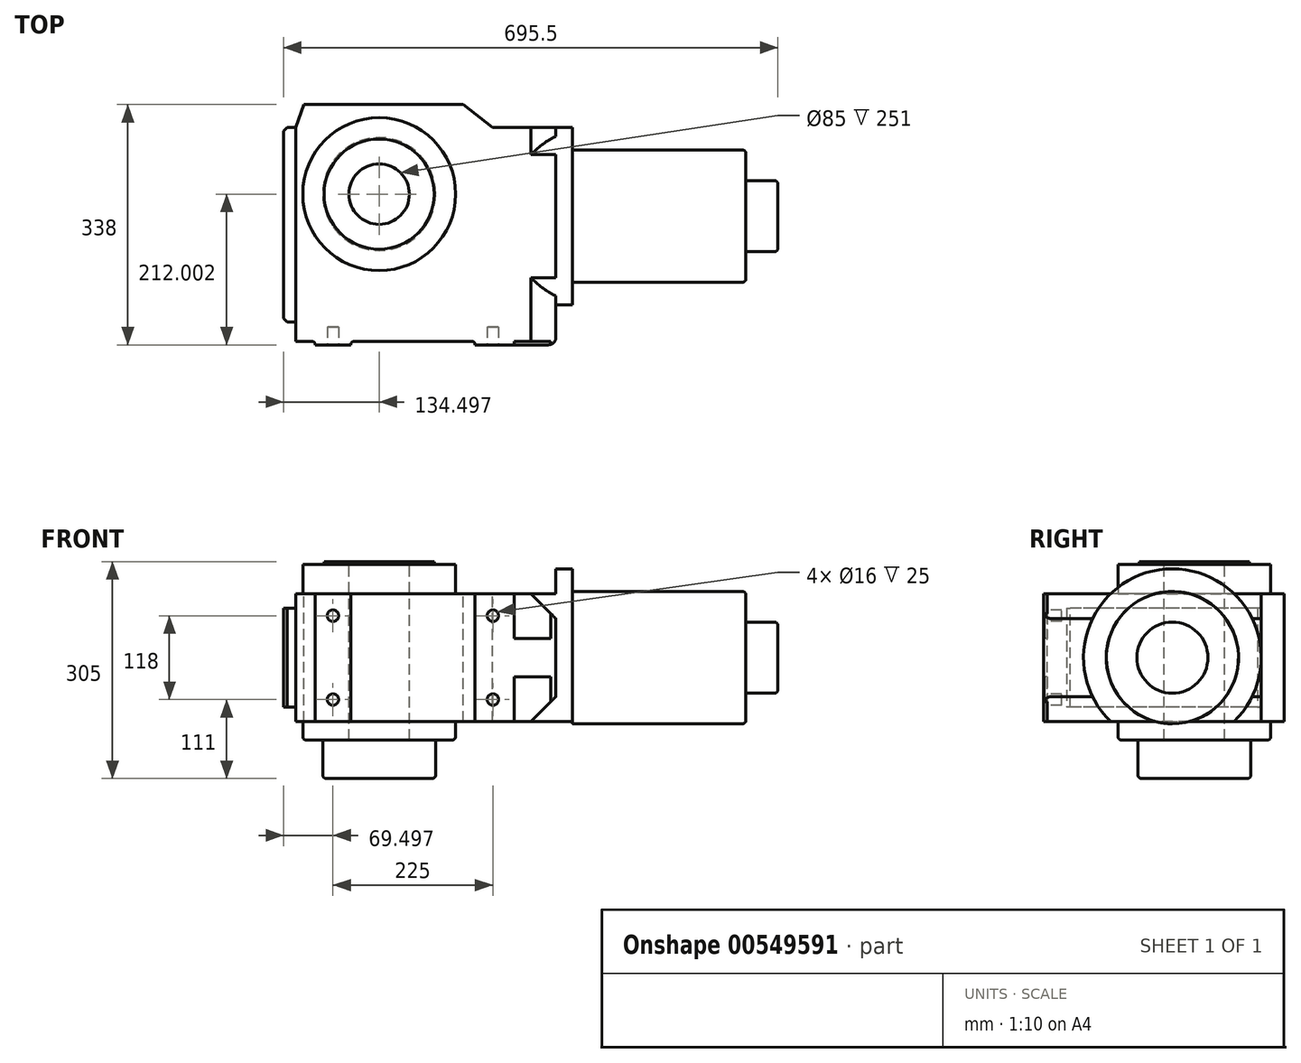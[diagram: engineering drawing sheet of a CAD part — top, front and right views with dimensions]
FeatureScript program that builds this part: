
annotation { "Feature Type Name" : "Feature", "Feature Type Description" : "" }
export const myFeature = defineFeature(function(context is Context, id is Id, definition is map)
    precondition{}
    {
        {
            var Q0;
            Q0=qCreatedBy(makeId("Top.planeOp"),FACE);
            var sketch = newSketch(context, id + "F0", { "sketchPlane" : qUnion([Q0])});
            skLineSegment(sketch, "E0.bottom", {"start": v(-178.5, 191.18) * mm, "end": v(187.5, 191.18) * mm});
            skLineSegment(sketch, "E0.top", {"start": v(-178.5, -146.82) * mm, "end": v(187.5, -146.82) * mm});
            skLineSegment(sketch, "E0.left", {"start": v(-178.5, 191.18) * mm, "end": v(-178.5, -146.82) * mm});
            skLineSegment(sketch, "E0.right", {"start": v(187.5, 191.18) * mm, "end": v(187.5, -146.82) * mm});
            skSolve(sketch);
        }
        {
            var Q0;
            Q0=makeQuery(id+"F0.imprint","IMPRINT",FACE,{"disambiguationData":[TD([[makeQuery(id+"F0.imprint","IMPRINT",EDGE,{"derivedFrom":sQuery(id+"F0.wireOp",EDGE,"E0.bottom")}),-1.0]])]});
            extrude(context, id + "F1", {"entities" : qUnion([Q0]), "oppositeDirection" : true, "depth" : 180 * mm, "offsetDistance" : 25 * mm});
        }
        {
            var Q0;
            Q0=makeQuery(id+"F1.opExtrude","CAP_FACE",FACE,{"disambiguationData":[OSD([sQuery(id+"F0.wireOp",EDGE,"E0.bottom"),sQuery(id+"F0.wireOp",EDGE,"E0.top"),sQuery(id+"F0.wireOp",EDGE,"E0.left"),sQuery(id+"F0.wireOp",EDGE,"E0.right")])],"isStart":true});
            var sketch = newSketch(context, id + "F2", { "sketchPlane" : qUnion([Q0])});
            skLineSegment(sketch, "E1", {"start": v(-252.27, 65.18) * mm, "end": v(288.5, 65.18) * mm, "construction": true});
            skLineSegment(sketch, "E2", {"start": v(-61, 181.9) * mm, "end": v(-61, -151.05) * mm, "construction": true});
            skCircle(sketch, "E3", {"center": v(-61, 65.18) * mm, "radius": 107.5 * mm});
            skSolve(sketch);
        }
        {
            var Q0;
            Q0=makeQuery(id+"F2.imprint","IMPRINT",FACE,{"disambiguationData":[TD([[makeQuery(id+"F2.imprint","IMPRINT",EDGE,{"derivedFrom":sQuery(id+"F2.wireOp",EDGE,"E3")}),1.0]])]});
            extrude(context, id + "F3", {"entities" : qUnion([Q0]), "operationType" : NewBodyOperationType.ADD, "depth" : 41 * mm, "offsetDistance" : 25 * mm});
        }
        {
            var Q0;
            Q0=makeQuery(id+"F1.opExtrude","CAP_FACE",FACE,{"disambiguationData":[OSD([sQuery(id+"F0.wireOp",EDGE,"E0.bottom"),sQuery(id+"F0.wireOp",EDGE,"E0.top"),sQuery(id+"F0.wireOp",EDGE,"E0.left"),sQuery(id+"F0.wireOp",EDGE,"E0.right")])],"isStart":true});
            var sketch = newSketch(context, id + "F4", { "sketchPlane" : qUnion([Q0])});
            skLineSegment(sketch, "E4", {"start": v(-178.5, -141.82) * mm, "end": v(-151, -141.82) * mm});
            skLineSegment(sketch, "E5", {"start": v(-151, -141.82) * mm, "end": v(-151, -146.82) * mm});
            skLineSegment(sketch, "E6", {"start": v(-101, -146.82) * mm, "end": v(-101, -141.82) * mm});
            skLineSegment(sketch, "E7", {"start": v(-101, -141.82) * mm, "end": v(74, -141.82) * mm});
            skLineSegment(sketch, "E8", {"start": v(74, -141.82) * mm, "end": v(74, -146.82) * mm});
            skSolve(sketch);
        }
        {
            var Q0;
            {var subQ0=sQuery(id+"F4.wireOp",EDGE,"E4");Q0=makeQuery(id+"F4.imprint","IMPRINT",FACE,{"disambiguationData":[TD([[makeQuery(id+"F4.imprint","IMPRINT",EDGE,{"derivedFrom":subQ0}),-1.0]])]});}
            var Q1;
            {var subQ0=sQuery(id+"F4.wireOp",EDGE,"E6");Q1=makeQuery(id+"F4.imprint","IMPRINT",FACE,{"disambiguationData":[TD([[makeQuery(id+"F4.imprint","IMPRINT",EDGE,{"derivedFrom":subQ0}),-1.0]])]});}
            extrude(context, id + "F5", {"entities" : qUnion([Q0, Q1]), "operationType" : NewBodyOperationType.REMOVE, "endBound" : BoundingType.THROUGH_ALL, "oppositeDirection" : true, "depth" : 25 * mm, "offsetDistance" : 25 * mm});
        }
        {
            var Q0;
            {var subQ0=sQuery(id+"F0.wireOp",EDGE,"E0.right");var subQ2=sQuery(id+"F0.wireOp",EDGE,"E0.top");Q0=makeQuery(id+"F5.boolean.opBoolean","SPLIT",FACE,{"disambiguationData":[TD([makeQuery(id+"F1.opExtrude","SWEPT_FACE",FACE,{"disambiguationData":[OSD([subQ0])]})])],"derivedFrom":makeQuery(id+"F1.opExtrude","SWEPT_FACE",FACE,{"disambiguationData":[OSD([subQ2])]})});}
            var sketch = newSketch(context, id + "F6", { "sketchPlane" : qUnion([Q0])});
            skLineSegment(sketch, "E9.bottom", {"start": v(129, 0) * mm, "end": v(180.7, 0) * mm});
            skLineSegment(sketch, "E9.top", {"start": v(129, -63) * mm, "end": v(180.7, -63) * mm});
            skLineSegment(sketch, "E9.left", {"start": v(129, 0) * mm, "end": v(129, -63) * mm});
            skLineSegment(sketch, "E9.right", {"start": v(180.7, 0) * mm, "end": v(180.7, -63) * mm});
            skLineSegment(sketch, "E10.bottom", {"start": v(129, -117) * mm, "end": v(180.7, -117) * mm});
            skLineSegment(sketch, "E10.top", {"start": v(129, -180) * mm, "end": v(180.7, -180) * mm});
            skLineSegment(sketch, "E10.left", {"start": v(129, -117) * mm, "end": v(129, -180) * mm});
            skLineSegment(sketch, "E10.right", {"start": v(180.7, -117) * mm, "end": v(180.7, -180) * mm});
            skSolve(sketch);
        }
        {
            var Q0;
            Q0=makeQuery(id+"F6.imprint","IMPRINT",FACE,{"disambiguationData":[TD([[makeQuery(id+"F6.imprint","IMPRINT",EDGE,{"derivedFrom":sQuery(id+"F6.wireOp",EDGE,"E9.bottom")}),-1.0]])]});
            var Q1;
            Q1=makeQuery(id+"F6.imprint","IMPRINT",FACE,{"disambiguationData":[TD([[makeQuery(id+"F6.imprint","IMPRINT",EDGE,{"derivedFrom":sQuery(id+"F6.wireOp",EDGE,"E10.bottom")}),-1.0]])]});
            extrude(context, id + "F7", {"entities" : qUnion([Q0, Q1]), "operationType" : NewBodyOperationType.REMOVE, "oppositeDirection" : true, "depth" : 5 * mm, "offsetDistance" : 25 * mm});
        }
        {
            var Q0;
            Q0=makeQuery(id+"F5.boolean.opBoolean","COPY",EDGE,{"derivedFrom":makeQuery(id+"F5.opExtrude","SWEPT_EDGE",EDGE,{"disambiguationData":[OSD([sQuery(id+"F4.wireOp",EDGE,"E4"),sQuery(id+"F4.wireOp",EDGE,"E5")])]})});
            var Q1;
            Q1=makeQuery(id+"F5.boolean.opBoolean","COPY",EDGE,{"derivedFrom":makeQuery(id+"F5.opExtrude","SWEPT_EDGE",EDGE,{"disambiguationData":[OSD([sQuery(id+"F4.wireOp",EDGE,"E6"),sQuery(id+"F4.wireOp",EDGE,"E7")])]})});
            var Q2;
            Q2=makeQuery(id+"F5.boolean.opBoolean","COPY",EDGE,{"derivedFrom":makeQuery(id+"F5.opExtrude","SWEPT_EDGE",EDGE,{"disambiguationData":[OSD([sQuery(id+"F4.wireOp",EDGE,"E7"),sQuery(id+"F4.wireOp",EDGE,"E8")])]})});
            fillet(context, id + "F8", {"entities" : qUnion([Q0, Q1, Q2]), "radius" : 5 * mm, "tangentPropagation" : true, "allowEdgeOverflow" : false});
        }
        {
            var Q0;
            Q0=makeQuery(id+"F1.opExtrude","SWEPT_EDGE",EDGE,{"disambiguationData":[OSD([sQuery(id+"F0.wireOp",EDGE,"E0.top"),sQuery(id+"F0.wireOp",EDGE,"E0.right")])]});
            fillet(context, id + "F9", {"entities" : qUnion([Q0]), "radius" : 10 * mm, "tangentPropagation" : true, "allowEdgeOverflow" : false});
        }
        {
            var Q0;
            Q0=makeQuery(id+"F1.opExtrude","SWEPT_FACE",FACE,{"disambiguationData":[OSD([sQuery(id+"F0.wireOp",EDGE,"E0.left")])]});
            var sketch = newSketch(context, id + "F10", { "sketchPlane" : qUnion([Q0])});
            skLineSegment(sketch, "E11.bottom", {"start": v(-159.18, -20.5) * mm, "end": v(114.82, -20.5) * mm});
            skLineSegment(sketch, "E11.top", {"start": v(-159.18, -159.5) * mm, "end": v(114.82, -159.5) * mm});
            skLineSegment(sketch, "E11.left", {"start": v(-159.18, -20.5) * mm, "end": v(-159.18, -159.5) * mm});
            skLineSegment(sketch, "E11.right", {"start": v(114.82, -20.5) * mm, "end": v(114.82, -159.5) * mm});
            skSolve(sketch);
        }
        {
            var Q0;
            Q0=makeQuery(id+"F10.imprint","IMPRINT",FACE,{"disambiguationData":[TD([[makeQuery(id+"F10.imprint","IMPRINT",EDGE,{"derivedFrom":sQuery(id+"F10.wireOp",EDGE,"E11.bottom")}),-1.0]])]});
            extrude(context, id + "F11", {"entities" : qUnion([Q0]), "operationType" : NewBodyOperationType.ADD, "depth" : 17 * mm, "offsetDistance" : 25 * mm});
        }
        {
            var Q0;
            Q0=makeQuery(id+"F1.opExtrude","CAP_FACE",FACE,{"disambiguationData":[OSD([sQuery(id+"F0.wireOp",EDGE,"E0.bottom"),sQuery(id+"F0.wireOp",EDGE,"E0.top"),sQuery(id+"F0.wireOp",EDGE,"E0.left"),sQuery(id+"F0.wireOp",EDGE,"E0.right")])],"isStart":false});
            var sketch = newSketch(context, id + "F12", { "sketchPlane" : qUnion([Q0])});
            skLineSegment(sketch, "E12", {"start": v(593.1, -65.18) * mm, "end": v(-643.77, -65.18) * mm, "construction": true});
            skLineSegment(sketch, "E13", {"start": v(-61, -619.27) * mm, "end": v(-61, 462.02) * mm, "construction": true});
            skCircle(sketch, "E14", {"center": v(-61, -65.18) * mm, "radius": 107.5 * mm});
            skSolve(sketch);
        }
        {
            var Q0;
            Q0=makeQuery(id+"F12.imprint","IMPRINT",FACE,{"disambiguationData":[TD([[makeQuery(id+"F12.imprint","IMPRINT",EDGE,{"derivedFrom":sQuery(id+"F12.wireOp",EDGE,"zn6HqGq0-Fjjd-aDj0-Oo1R-vwsV0e5vIUza")}),1.0]])]});
            var Q1;
            Q1=makeQuery(id+"F12.imprint","IMPRINT",FACE,{"disambiguationData":[TD([[makeQuery(id+"F12.imprint","IMPRINT",EDGE,{"derivedFrom":sQuery(id+"F12.wireOp",EDGE,"E14")}),1.0]])]});
            extrude(context, id + "F13", {"entities" : qUnion([Q0, Q1]), "operationType" : NewBodyOperationType.ADD, "depth" : 26 * mm, "offsetDistance" : 25 * mm});
        }
        {
            var Q0;
            Q0=makeQuery(id+"F1.opExtrude","CAP_FACE",FACE,{"disambiguationData":[OSD([sQuery(id+"F0.wireOp",EDGE,"E0.bottom"),sQuery(id+"F0.wireOp",EDGE,"E0.top"),sQuery(id+"F0.wireOp",EDGE,"E0.left"),sQuery(id+"F0.wireOp",EDGE,"E0.right")])],"isStart":true});
            var sketch = newSketch(context, id + "F14", { "sketchPlane" : qUnion([Q0])});
            skLineSegment(sketch, "E15.bottom", {"start": v(98.3, 191.18) * mm, "end": v(187.5, 191.18) * mm});
            skLineSegment(sketch, "E15.top", {"start": v(98.3, 159.18) * mm, "end": v(187.5, 159.18) * mm});
            skLineSegment(sketch, "E15.left", {"start": v(98.3, 191.18) * mm, "end": v(98.3, 159.18) * mm});
            skLineSegment(sketch, "E15.right", {"start": v(187.5, 191.18) * mm, "end": v(187.5, 159.18) * mm});
            skLineSegment(sketch, "E16", {"start": v(-166.85, 191.18) * mm, "end": v(-178.5, 159.13) * mm});
            skLineSegment(sketch, "E17", {"start": v(98.3, 159.18) * mm, "end": v(57.5, 191.18) * mm});
            skSolve(sketch);
        }
        {
            var Q0;
            Q0=makeQuery(id+"F14.imprint","IMPRINT",FACE,{"disambiguationData":[TD([[makeQuery(id+"F14.imprint","IMPRINT",EDGE,{"derivedFrom":sQuery(id+"F14.wireOp",EDGE,"E15.bottom")}),-1.0]])]});
            var Q1;
            {var subQ0=sQuery(id+"F14.wireOp",EDGE,"E15.left");Q1=makeQuery(id+"F14.imprint","IMPRINT",FACE,{"disambiguationData":[TD([[makeQuery(id+"F14.imprint","IMPRINT",EDGE,{"derivedFrom":subQ0}),-1.0]])]});}
            var Q2;
            {var subQ0=sQuery(id+"F14.wireOp",EDGE,"E16");Q2=makeQuery(id+"F14.imprint","IMPRINT",FACE,{"disambiguationData":[TD([[makeQuery(id+"F14.imprint","IMPRINT",EDGE,{"derivedFrom":subQ0}),-1.0]])]});}
            extrude(context, id + "F15", {"entities" : qUnion([Q0, Q1, Q2]), "operationType" : NewBodyOperationType.REMOVE, "endBound" : BoundingType.THROUGH_ALL, "oppositeDirection" : true, "depth" : 25 * mm, "offsetDistance" : 25 * mm});
        }
        {
            var Q0;
            Q0=makeQuery(id+"F11.opExtrude","CAP_EDGE",EDGE,{"disambiguationData":[OSD([sQuery(id+"F10.wireOp",EDGE,"E11.left")])],"isStart":false});
            chamfer(context, id + "F16", {"entities" : qUnion([Q0]), "width" : 5 * mm, "tangentPropagation" : true});
        }
        {
            var Q0;
            Q0=makeQuery(id+"F11.opExtrude","CAP_EDGE",EDGE,{"disambiguationData":[OSD([sQuery(id+"F10.wireOp",EDGE,"E11.right")])],"isStart":false});
            chamfer(context, id + "F17", {"entities" : qUnion([Q0]), "width" : 5 * mm, "tangentPropagation" : true});
        }
        {
            var Q0;
            Q0=makeQuery(id+"F1.opExtrude","SWEPT_FACE",FACE,{"disambiguationData":[OSD([sQuery(id+"F0.wireOp",EDGE,"E0.right")])]});
            var sketch = newSketch(context, id + "F18", { "sketchPlane" : qUnion([Q0])});
            skCircle(sketch, "E18", {"center": v(34.18, -90) * mm, "radius": 125 * mm});
            skPoint(sketch, "E18.centerSnap0", {"position": v(159.18, -90) * mm});
            skSolve(sketch);
        }
        {
            var Q0;
            {var subQ0=sQuery(id+"F18.wireOp",EDGE,"E18");var subQ1=makeQuery(id+"F1.opExtrude","CAP_EDGE",EDGE,{"disambiguationData":[OSD([sQuery(id+"F0.wireOp",EDGE,"E0.right")])],"isStart":false});var subQ2=makeQuery(id+"F18.imprint","INTERSECT",VERTEX,{"disambiguationData":[OD(0.0)],"derivedFrom":[subQ1,subQ0]});Q0=makeQuery(id+"F18.imprint","IMPRINT",FACE,{"disambiguationData":[TD([[makeQuery(id+"F18.imprint","IMPRINT",EDGE,{"disambiguationData":[TD([[subQ2,-1.0]])],"derivedFrom":subQ0}),1.0]])]});}
            var Q1;
            {var subQ0=sQuery(id+"F18.wireOp",EDGE,"E18");var subQ1=makeQuery(id+"F1.opExtrude","CAP_EDGE",EDGE,{"disambiguationData":[OSD([sQuery(id+"F0.wireOp",EDGE,"E0.right")])],"isStart":true});var subQ2=makeQuery(id+"F18.imprint","INTERSECT",VERTEX,{"disambiguationData":[OD(0.0)],"derivedFrom":[subQ1,subQ0]});Q1=makeQuery(id+"F18.imprint","IMPRINT",FACE,{"disambiguationData":[TD([[makeQuery(id+"F18.imprint","IMPRINT",EDGE,{"disambiguationData":[TD([[subQ2,-1.0]])],"derivedFrom":subQ0}),1.0]])]});}
            var Q2;
            {var subQ0=sQuery(id+"F18.wireOp",EDGE,"E18");var subQ1=sQuery(id+"F0.wireOp",EDGE,"E0.right");var subQ5=makeQuery(id+"F1.opExtrude","CAP_EDGE",EDGE,{"disambiguationData":[OSD([subQ1])],"isStart":true});var subQ6=makeQuery(id+"F18.imprint","INTERSECT",VERTEX,{"disambiguationData":[OD(1.0)],"derivedFrom":[subQ5,subQ0]});Q2=makeQuery(id+"F18.imprint","IMPRINT",FACE,{"disambiguationData":[TD([[makeQuery(id+"F18.imprint","IMPRINT",EDGE,{"disambiguationData":[TD([[subQ6,-1.0]])],"derivedFrom":subQ0}),1.0]])]});}
            extrude(context, id + "F19", {"entities" : qUnion([Q0, Q1, Q2]), "operationType" : NewBodyOperationType.ADD, "depth" : 23.5 * mm, "offsetDistance" : 25 * mm});
        }
        {
            var Q0;
            {var subQ0=sQuery(id+"F0.wireOp",EDGE,"E0.right");Q0=makeQuery(id+"F19.boolean.opBoolean","SPLIT",EDGE,{"disambiguationData":[topologyDisambiguationEdgeConnected([makeQuery(id+"F1.opExtrude","CAP_FACE",FACE,{"disambiguationData":[OSD([sQuery(id+"F0.wireOp",EDGE,"E0.bottom"),sQuery(id+"F0.wireOp",EDGE,"E0.top"),sQuery(id+"F0.wireOp",EDGE,"E0.left"),subQ0])],"isStart":false}),makeQuery(id+"F19.opExtrude","CAP_FACE",FACE,{"disambiguationData":[OSD([sQuery(id+"F18.wireOp",EDGE,"E18")])],"isStart":true})])],"derivedFrom":makeQuery(id+"F1.opExtrude","CAP_EDGE",EDGE,{"disambiguationData":[OSD([subQ0])],"isStart":false})});}
            var Q1;
            {var subQ0=sQuery(id+"F0.wireOp",EDGE,"E0.right");Q1=makeQuery(id+"F19.boolean.opBoolean","SPLIT",EDGE,{"disambiguationData":[topologyDisambiguationEdgeConnected([makeQuery(id+"F1.opExtrude","CAP_FACE",FACE,{"disambiguationData":[OSD([sQuery(id+"F0.wireOp",EDGE,"E0.bottom"),sQuery(id+"F0.wireOp",EDGE,"E0.top"),sQuery(id+"F0.wireOp",EDGE,"E0.left"),subQ0])],"isStart":true}),makeQuery(id+"F19.opExtrude","CAP_FACE",FACE,{"disambiguationData":[OSD([sQuery(id+"F18.wireOp",EDGE,"E18")])],"isStart":true})])],"derivedFrom":makeQuery(id+"F1.opExtrude","CAP_EDGE",EDGE,{"disambiguationData":[OSD([subQ0])],"isStart":true})});}
            chamfer(context, id + "F20", {"entities" : qUnion([Q0, Q1]), "width" : 35 * mm, "tangentPropagation" : true});
        }
        {
            var Q0;
            Q0=makeQuery(id+"F19.opExtrude","CAP_FACE",FACE,{"disambiguationData":[OSD([sQuery(id+"F18.wireOp",EDGE,"E18")])],"isStart":false});
            var sketch = newSketch(context, id + "F21", { "sketchPlane" : qUnion([Q0])});
            skCircle(sketch, "E19", {"center": v(34.18, -90) * mm, "radius": 93 * mm});
            skSolve(sketch);
        }
        {
            var Q0;
            Q0=makeQuery(id+"F21.imprint","IMPRINT",FACE,{"disambiguationData":[TD([[makeQuery(id+"F21.imprint","IMPRINT",EDGE,{"derivedFrom":sQuery(id+"F21.wireOp",EDGE,"E19")}),1.0]])]});
            extrude(context, id + "F22", {"entities" : qUnion([Q0]), "operationType" : NewBodyOperationType.ADD, "depth" : 244 * mm, "offsetDistance" : 25 * mm});
        }
        {
            var Q0;
            Q0=makeQuery(id+"F22.opExtrude","CAP_FACE",FACE,{"disambiguationData":[OSD([sQuery(id+"F21.wireOp",EDGE,"E19")])],"isStart":false});
            var sketch = newSketch(context, id + "F23", { "sketchPlane" : qUnion([Q0])});
            skCircle(sketch, "E20", {"center": v(34.18, -90) * mm, "radius": 50 * mm});
            skSolve(sketch);
        }
        {
            var Q0;
            Q0=makeQuery(id+"F23.imprint","IMPRINT",FACE,{"disambiguationData":[TD([[makeQuery(id+"F23.imprint","IMPRINT",EDGE,{"derivedFrom":sQuery(id+"F23.wireOp",EDGE,"E20")}),1.0]])]});
            extrude(context, id + "F24", {"entities" : qUnion([Q0]), "operationType" : NewBodyOperationType.ADD, "depth" : 45 * mm, "offsetDistance" : 25 * mm});
        }
        {
            var Q0;
            Q0=makeQuery(id+"F24.opExtrude","CAP_EDGE",EDGE,{"disambiguationData":[OSD([sQuery(id+"F23.wireOp",EDGE,"E20")])],"isStart":false});
            var Q1;
            Q1=makeQuery(id+"F22.opExtrude","CAP_EDGE",EDGE,{"disambiguationData":[OSD([sQuery(id+"F21.wireOp",EDGE,"E19")])],"isStart":false});
            fillet(context, id + "F25", {"entities" : qUnion([Q0, Q1]), "radius" : 5 * mm, "tangentPropagation" : true, "allowEdgeOverflow" : false});
        }
        {
            var Q0;
            Q0=makeQuery(id+"F3.opExtrude","CAP_FACE",FACE,{"disambiguationData":[OSD([sQuery(id+"F2.wireOp",EDGE,"E3")])],"isStart":false});
            var sketch = newSketch(context, id + "F26", { "sketchPlane" : qUnion([Q0])});
            skCircle(sketch, "E21", {"center": v(-61, 65.18) * mm, "radius": 42.5 * mm});
            skSolve(sketch);
        }
        {
            var Q0;
            Q0=makeQuery(id+"F26.imprint","IMPRINT",FACE,{"disambiguationData":[TD([[makeQuery(id+"F26.imprint","IMPRINT",EDGE,{"derivedFrom":sQuery(id+"F26.wireOp",EDGE,"E21")}),1.0]])]});
            extrude(context, id + "F27", {"entities" : qUnion([Q0]), "operationType" : NewBodyOperationType.REMOVE, "oppositeDirection" : true, "depth" : 250 * mm, "offsetDistance" : 25 * mm});
        }
        {
            var Q0;
            {var subQ2=sQuery(id+"F0.wireOp",EDGE,"E0.top");Q0=makeQuery(id+"F5.boolean.opBoolean","SPLIT",FACE,{"disambiguationData":[TD([makeQuery(id+"F5.opExtrude","SWEPT_FACE",FACE,{"disambiguationData":[OSD([sQuery(id+"F4.wireOp",EDGE,"E5")])]})])],"derivedFrom":makeQuery(id+"F1.opExtrude","SWEPT_FACE",FACE,{"disambiguationData":[OSD([subQ2])]})});}
            var sketch = newSketch(context, id + "F28", { "sketchPlane" : qUnion([Q0])});
            skLineSegment(sketch, "E22", {"start": v(-271.6, -31) * mm, "end": v(364.41, -31) * mm, "construction": true});
            skLineSegment(sketch, "E23", {"start": v(-258.39, -149) * mm, "end": v(373, -149) * mm, "construction": true});
            skLineSegment(sketch, "E24", {"start": v(-126, 98.91) * mm, "end": v(-126, -299.34) * mm, "construction": true});
            skLineSegment(sketch, "E25", {"start": v(99, 105.52) * mm, "end": v(99, -301.32) * mm, "construction": true});
            skCircle(sketch, "E26", {"center": v(-126, -31) * mm, "radius": 8 * mm});
            skCircle(sketch, "E27", {"center": v(-126, -149) * mm, "radius": 8 * mm});
            skCircle(sketch, "E28", {"center": v(99, -31) * mm, "radius": 8 * mm});
            skCircle(sketch, "E29", {"center": v(99, -149) * mm, "radius": 8 * mm});
            skSolve(sketch);
        }
        {
            var Q0;
            Q0=makeQuery(id+"F28.imprint","IMPRINT",FACE,{"disambiguationData":[TD([[makeQuery(id+"F28.imprint","IMPRINT",EDGE,{"derivedFrom":sQuery(id+"F28.wireOp",EDGE,"E26")}),1.0]])]});
            var Q1;
            Q1=makeQuery(id+"F28.imprint","IMPRINT",FACE,{"disambiguationData":[TD([[makeQuery(id+"F28.imprint","IMPRINT",EDGE,{"derivedFrom":sQuery(id+"F28.wireOp",EDGE,"E27")}),1.0]])]});
            var Q2;
            Q2=makeQuery(id+"F28.imprint","IMPRINT",FACE,{"disambiguationData":[TD([[makeQuery(id+"F28.imprint","IMPRINT",EDGE,{"derivedFrom":sQuery(id+"F28.wireOp",EDGE,"E29")}),1.0]])]});
            var Q3;
            Q3=makeQuery(id+"F28.imprint","IMPRINT",FACE,{"disambiguationData":[TD([[makeQuery(id+"F28.imprint","IMPRINT",EDGE,{"derivedFrom":sQuery(id+"F28.wireOp",EDGE,"E28")}),1.0]])]});
            extrude(context, id + "F29", {"entities" : qUnion([Q0, Q1, Q2, Q3]), "operationType" : NewBodyOperationType.REMOVE, "oppositeDirection" : true, "depth" : 25 * mm, "offsetDistance" : 25 * mm});
        }
        {
            var Q0;
            Q0=makeQuery(id+"F13.opExtrude","CAP_FACE",FACE,{"disambiguationData":[OSD([sQuery(id+"F12.wireOp",EDGE,"E14")])],"isStart":false});
            var sketch = newSketch(context, id + "F30", { "sketchPlane" : qUnion([Q0])});
            skCircle(sketch, "E30", {"center": v(-61, -65.18) * mm, "radius": 79.5 * mm});
            skSolve(sketch);
        }
        {
            var Q0;
            Q0=makeQuery(id+"F30.imprint","IMPRINT",FACE,{"disambiguationData":[TD([[makeQuery(id+"F30.imprint","IMPRINT",EDGE,{"derivedFrom":sQuery(id+"F30.wireOp",EDGE,"E30")}),1.0]])]});
            var Q1;
            Q1=makeQuery(id+"F30.imprint","IMPRINT",FACE,{"disambiguationData":[TD([[makeQuery(id+"F30.imprint","IMPRINT",EDGE,{"derivedFrom":makeQuery(id+"F27.boolean.opBoolean","INTERSECT",EDGE,{"derivedFrom":[makeQuery(id+"F13.opExtrude","CAP_FACE",FACE,{"disambiguationData":[OSD([sQuery(id+"F12.wireOp",EDGE,"E14")])],"isStart":false}),makeQuery(id+"F27.opExtrude","SWEPT_FACE",FACE,{"disambiguationData":[OSD([sQuery(id+"F26.wireOp",EDGE,"E21")])]})]})}),1.0]])]});
            extrude(context, id + "F31", {"entities" : qUnion([Q0, Q1]), "operationType" : NewBodyOperationType.ADD, "depth" : 54 * mm, "offsetDistance" : 25 * mm});
        }
        {
            var Q0;
            Q0=makeQuery(id+"F13.opExtrude","CAP_EDGE",EDGE,{"disambiguationData":[OSD([sQuery(id+"F12.wireOp",EDGE,"E14")])],"isStart":false});
            var Q1;
            Q1=makeQuery(id+"F31.opExtrude","CAP_EDGE",EDGE,{"disambiguationData":[OSD([sQuery(id+"F30.wireOp",EDGE,"E30")])],"isStart":false});
            fillet(context, id + "F32", {"entities" : qUnion([Q0, Q1]), "radius" : 5 * mm, "tangentPropagation" : true, "allowEdgeOverflow" : false});
        }
        {
            var Q0;
            Q0=makeQuery(id+"F3.opExtrude","CAP_FACE",FACE,{"disambiguationData":[OSD([sQuery(id+"F2.wireOp",EDGE,"E3")])],"isStart":false});
            var sketch = newSketch(context, id + "F33", { "sketchPlane" : qUnion([Q0])});
            skCircle(sketch, "E31", {"center": v(-61, 65.18) * mm, "radius": 77.5 * mm});
            skSolve(sketch);
        }
        {
            var Q0;
            Q0=makeQuery(id+"F33.imprint","IMPRINT",FACE,{"disambiguationData":[TD([[makeQuery(id+"F33.imprint","IMPRINT",EDGE,{"derivedFrom":sQuery(id+"F33.wireOp",EDGE,"E31")}),1.0]])]});
            extrude(context, id + "F34", {"entities" : qUnion([Q0]), "operationType" : NewBodyOperationType.ADD, "depth" : 4 * mm, "offsetDistance" : 25 * mm});
        }
    });
